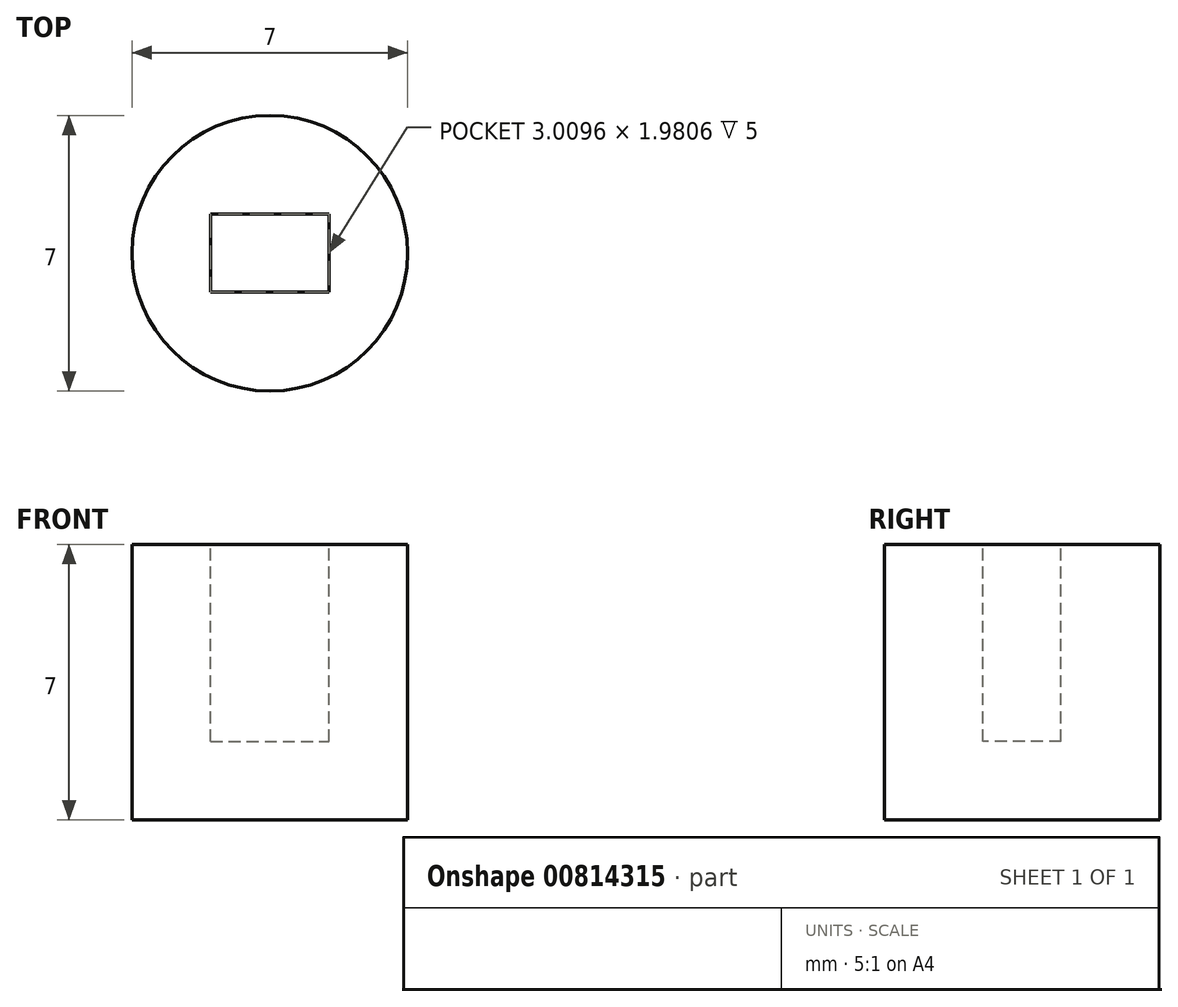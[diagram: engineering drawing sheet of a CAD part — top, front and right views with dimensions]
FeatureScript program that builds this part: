
annotation { "Feature Type Name" : "Feature", "Feature Type Description" : "" }
export const myFeature = defineFeature(function(context is Context, id is Id, definition is map)
    precondition{}
    {
        {
            var Q0;
            Q0=qCreatedBy(makeId("Top.planeOp"),FACE);
            var sketch = newSketch(context, id + "F0", { "sketchPlane" : qUnion([Q0])});
            skCircle(sketch, "E0", {"center": v(0, 0) * mm, "radius": 3.5 * mm});
            skSolve(sketch);
        }
        {
            var Q0;
            Q0=qSketchRegion(id+"F0",true);
            extrude(context, id + "F1", {"entities" : qUnion([Q0]), "depth" : 7 * mm, "offsetDistance" : 25.4 * mm});
        }
        {
            var Q0;
            Q0=makeQuery(id+"F1.opExtrude","CAP_FACE",FACE,{"disambiguationData":[OSD([sQuery(id+"F0.wireOp",EDGE,"E0")])],"isStart":false});
            var sketch = newSketch(context, id + "F2", { "sketchPlane" : qUnion([Q0])});
            skLineSegment(sketch, "E1.bottom", {"start": v(-1.5, 1) * mm, "end": v(1.5, 1) * mm});
            skLineSegment(sketch, "E1.top", {"start": v(-1.5, -1) * mm, "end": v(1.5, -1) * mm});
            skLineSegment(sketch, "E1.left", {"start": v(-1.5, 1) * mm, "end": v(-1.5, -1) * mm});
            skLineSegment(sketch, "E1.right", {"start": v(1.5, 1) * mm, "end": v(1.5, -1) * mm});
            skPoint(sketch, "E1.middle", {"position": v(0, 0) * mm});
            skSolve(sketch);
        }
        {
            var Q0;
            Q0=qSketchRegion(id+"F2",true);
            extrude(context, id + "F3", {"entities" : qUnion([Q0]), "operationType" : NewBodyOperationType.REMOVE, "oppositeDirection" : true, "depth" : 5 * mm, "offsetDistance" : 25.4 * mm});
        }
    });
